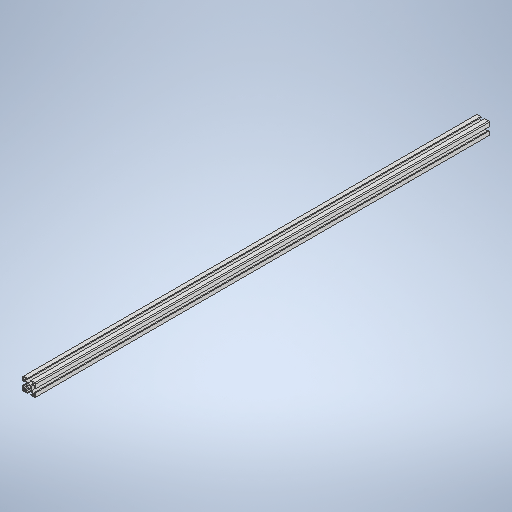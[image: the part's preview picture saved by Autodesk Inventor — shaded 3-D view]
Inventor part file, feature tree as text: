
AUTODESK INVENTOR PART (.ipt)
format: ipt  version: 2025 (Build 290162000, 162)  size: 314,880 bytes
history: native  units: in
note: dims shown in document units (in); Inventor stores cm internally (conversion verified against a paired STEP export)
features: extrude x1, sketch x1
ambient origin geometry x8: Origin, YZ Plane, XZ Plane, XY Plane, X Axis, Y Axis, Z Axis, Center Point
bodies: Solid1 (feature_tree)
feature tree (2):
  extrude  "Extrusion1"  Depth=41.1024in
  sketch  "Sketch1"  dims[d6=41.1024in d7=0.0in d8=0.1969in d9=0.0344in]
